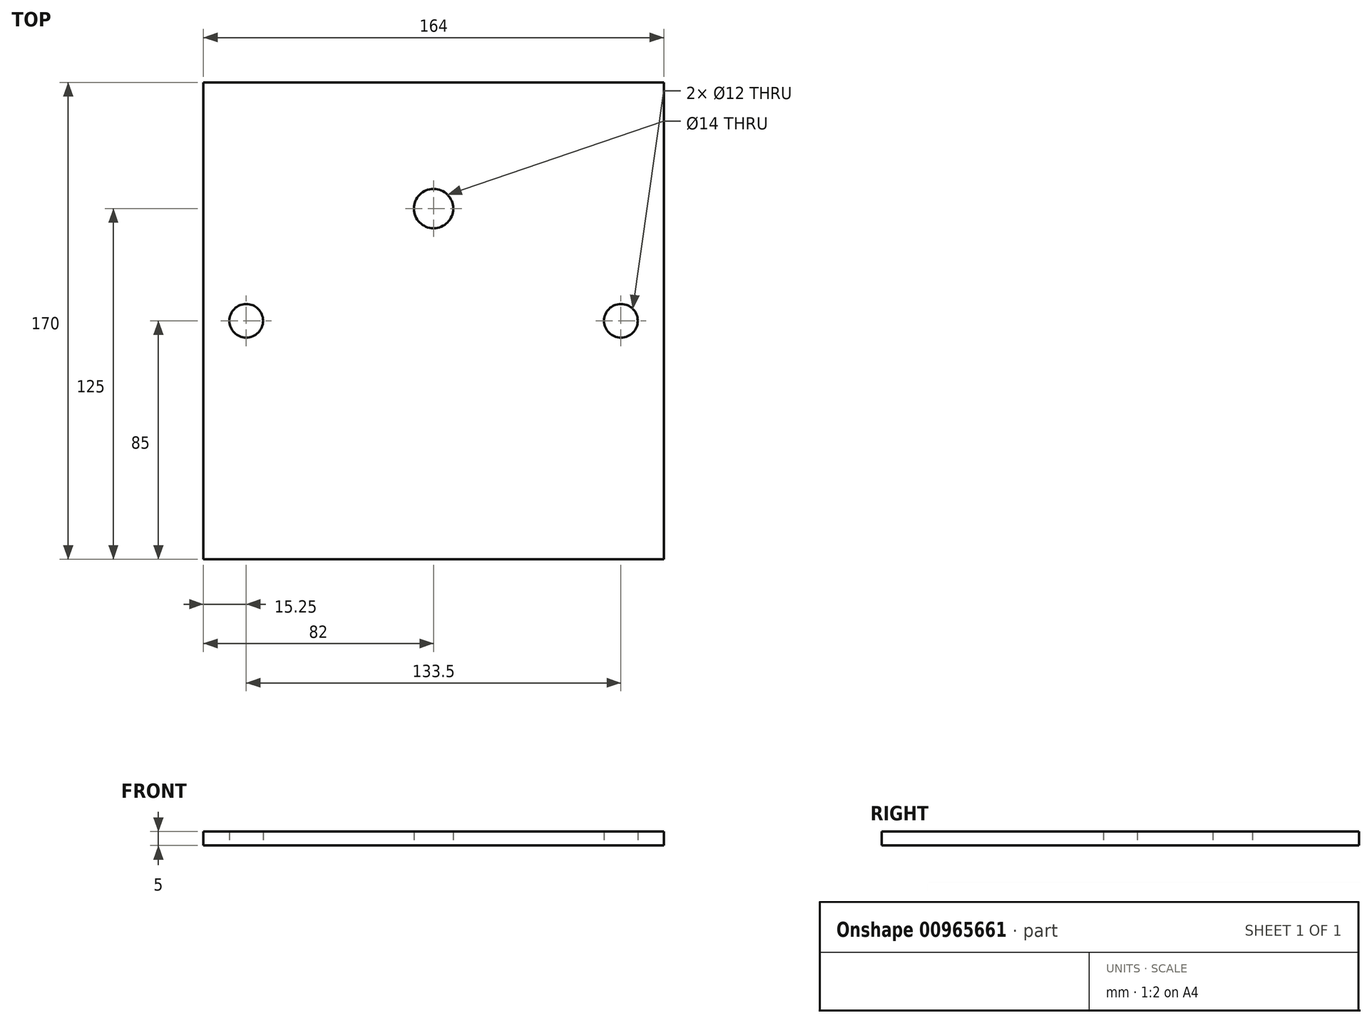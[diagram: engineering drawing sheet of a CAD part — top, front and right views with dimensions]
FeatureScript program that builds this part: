
annotation { "Feature Type Name" : "Feature", "Feature Type Description" : "" }
export const myFeature = defineFeature(function(context is Context, id is Id, definition is map)
    precondition{}
    {
        {
            var Q0;
            Q0=qCreatedBy(makeId("Top.planeOp"),FACE);
            var sketch = newSketch(context, id + "F0", { "sketchPlane" : qUnion([Q0])});
            skLineSegment(sketch, "E0.bottom", {"start": v(82, -85) * mm, "end": v(-82, -85) * mm});
            skLineSegment(sketch, "E0.top", {"start": v(82, 85) * mm, "end": v(-82, 85) * mm});
            skLineSegment(sketch, "E0.left", {"start": v(82, -85) * mm, "end": v(82, 85) * mm});
            skLineSegment(sketch, "E0.right", {"start": v(-82, -85) * mm, "end": v(-82, 85) * mm});
            skPoint(sketch, "E0.middle", {"position": v(0, 0) * mm});
            skCircle(sketch, "E1", {"center": v(-66.75, 0) * mm, "radius": 6 * mm});
            skCircle(sketch, "E2", {"center": v(66.75, 0) * mm, "radius": 6 * mm});
            skCircle(sketch, "E3", {"center": v(0, 40) * mm, "radius": 7 * mm});
            skSolve(sketch);
        }
        {
            var Q0;
            Q0=makeQuery(id+"F0.imprint","IMPRINT",FACE,{"disambiguationData":[TD([[makeQuery(id+"F0.imprint","IMPRINT",EDGE,{"derivedFrom":sQuery(id+"F0.wireOp",EDGE,"E0.bottom")}),-1.0]])]});
            extrude(context, id + "F1", {"entities" : qUnion([Q0]), "depth" : 5 * mm, "offsetDistance" : 25 * mm});
        }
        {
            var Q0;
            Q0=makeQuery(id+"F1.opExtrude","SWEPT_FACE",FACE,{"disambiguationData":[OSD([sQuery(id+"F0.wireOp",EDGE,"E0.top")])]});
            var sketch = newSketch(context, id + "F2", { "sketchPlane" : qUnion([Q0])});
            skLineSegment(sketch, "E4.bottom", {"start": v(-82, 5) * mm, "end": v(-62, 5) * mm});
            skLineSegment(sketch, "E4.top", {"start": v(-82, 0) * mm, "end": v(-62, 0) * mm});
            skLineSegment(sketch, "E4.left", {"start": v(-82, 5) * mm, "end": v(-82, 0) * mm});
            skLineSegment(sketch, "E4.right", {"start": v(-62, 5) * mm, "end": v(-62, 0) * mm});
            skLineSegment(sketch, "E5.bottom", {"start": v(82, 5) * mm, "end": v(62, 5) * mm});
            skLineSegment(sketch, "E5.top", {"start": v(82, 0) * mm, "end": v(62, 0) * mm});
            skLineSegment(sketch, "E5.left", {"start": v(82, 5) * mm, "end": v(82, 0) * mm});
            skLineSegment(sketch, "E5.right", {"start": v(62, 5) * mm, "end": v(62, 0) * mm});
            skSolve(sketch);
        }
        {
            var Q0;
            Q0=makeQuery(id+"F2.imprint","IMPRINT",FACE,{"disambiguationData":[TD([[makeQuery(id+"F2.imprint","IMPRINT",EDGE,{"derivedFrom":sQuery(id+"F2.wireOp",EDGE,"E5.bottom")}),-1.0]])]});
            var Q1;
            Q1=makeQuery(id+"F2.imprint","IMPRINT",FACE,{"disambiguationData":[TD([[makeQuery(id+"F2.imprint","IMPRINT",EDGE,{"derivedFrom":sQuery(id+"F2.wireOp",EDGE,"E4.bottom")}),-1.0]])]});
            extrude(context, id + "F3", {"entities" : qUnion([Q0, Q1]), "operationType" : NewBodyOperationType.ADD, "oppositeDirection" : true, "depth" : 0.01 * mm, "offsetDistance" : 25 * mm});
        }
    });
